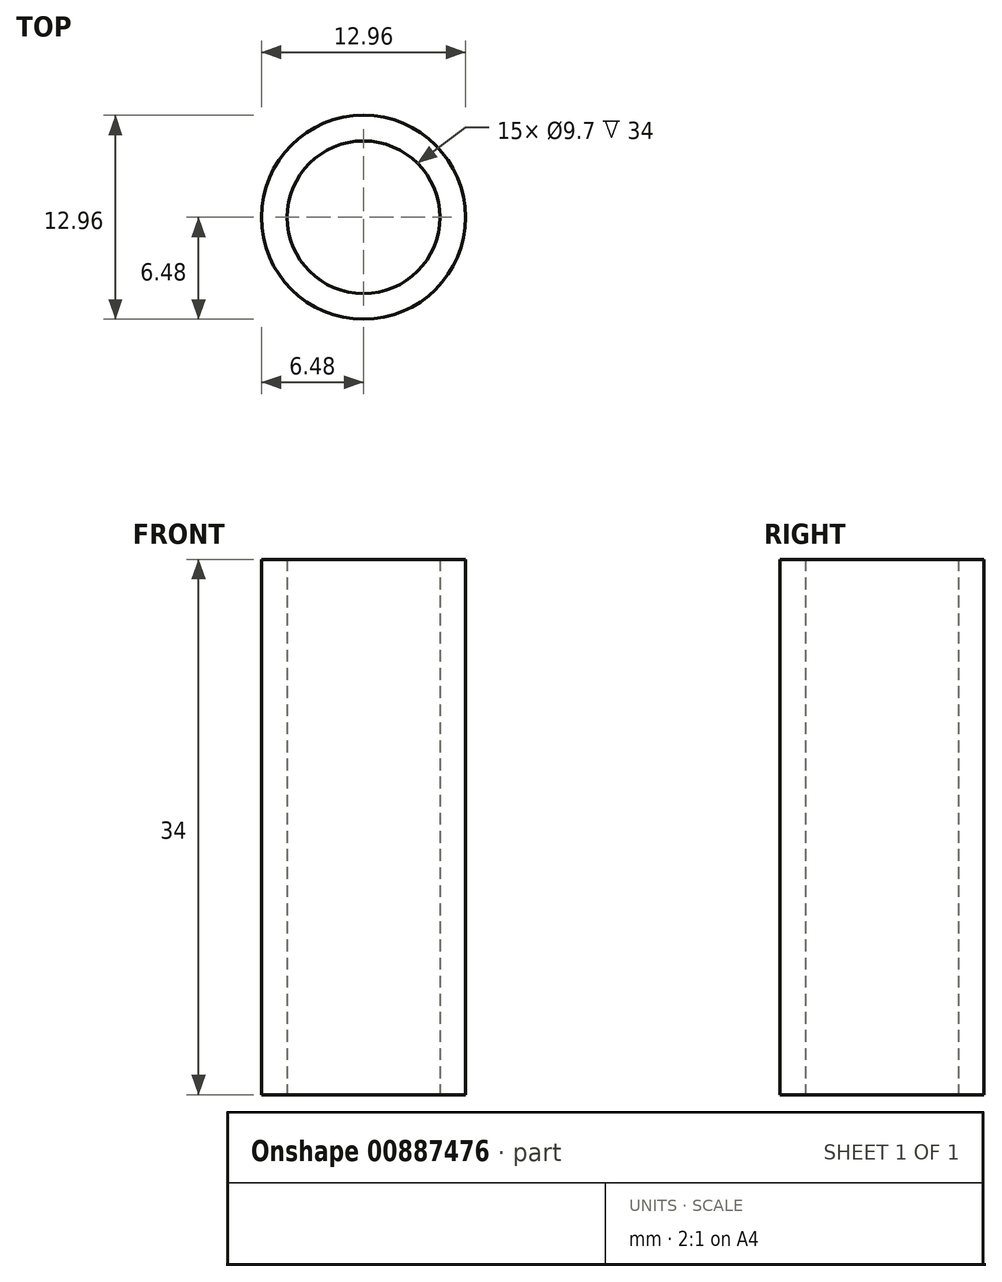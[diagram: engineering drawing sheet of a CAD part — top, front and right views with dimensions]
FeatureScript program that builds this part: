
annotation { "Feature Type Name" : "Feature", "Feature Type Description" : "" }
export const myFeature = defineFeature(function(context is Context, id is Id, definition is map)
    precondition{}
    {
        {
            var Q0;
            Q0=qCreatedBy(makeId("Top.planeOp"),FACE);
            var sketch = newSketch(context, id + "F0", { "sketchPlane" : qUnion([Q0])});
            skCircle(sketch, "E0", {"center": v(0, 0) * mm, "radius": 6.48 * mm});
            skCircle(sketch, "E1", {"center": v(0, 0) * mm, "radius": 4.85 * mm});
            skSolve(sketch);
        }
        {
            var Q0;
            Q0 = qSketchRegion(id + "F0", true);
            extrude(context, id + "F1", {"entities" : qUnion([Q0]), "depth" : 34 * mm, "offsetDistance" : 25 * mm});
        }
    });
